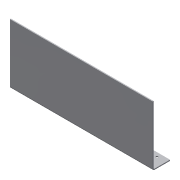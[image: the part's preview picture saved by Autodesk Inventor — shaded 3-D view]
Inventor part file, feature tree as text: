
AUTODESK INVENTOR PART (.ipt)
format: ipt  version: 2016 SP2 (Build 200236200, 236)  size: 241,664 bytes
history: native  units: in
note: dims shown in document units (in); Inventor stores cm internally (conversion verified against a paired STEP export)
features: sheet_metal_op x4, sketch x4, other x3, reference x2, hole x1, mirror x1
ambient origin geometry x8: Origin, YZ Plane, XZ Plane, XY Plane, X Axis, Y Axis, Z Axis, Center Point
bodies: Solid1 (feature_tree)
feature tree (15):
  sheet_metal_op  "Face1"
  sheet_metal_op  "Flange1"
  hole  "Hole1"  [1 undecoded]
  mirror  "Mirror1"
  sketch  "Sketch1"  dims[d0=11.1811in d1=4.7244in]
  other  "Plate1"
  sketch  "Sketch2"  dims[d2=0.0787in]
  other  "Plate2"
  sheet_metal_op  "Bend1"
  sheet_metal_op  "Corner1"
  sketch  "Sketch5"  dims[d3=0.0787in]
  sketch  "Sketch6"  dims[d4=0.0394in d5=0.1575in d6=0.0787in d7=1.378in d8=90.0deg d9=0.0787in d10=0.315in d11=0.0787in d12=0.0787in d15=0.0787in d16=0.0in d17=0.315in d18=0.7087in d19=0.1693in d20=0.2362in d21=0.1575in d22=0.0787in d23=90.0deg d24=0.0787in d25=0.8108in d26=2.7559in]
  reference  "Reference7"
  reference  "Reference8"
  other  "Cut1"
note: 1 required parameter value undecoded (feature->parameter linkage not recoverable at this tier; creation-order binding heuristic only, values carry confidence <= 0.55)
